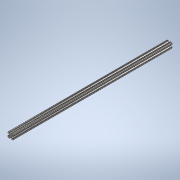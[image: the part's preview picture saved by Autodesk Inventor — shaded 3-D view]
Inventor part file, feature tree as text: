
AUTODESK INVENTOR PART (.ipt)
format: ipt  version: 2020 (Build 240168000, 168)  size: 238,080 bytes
history: native  units: in
note: dims shown in document units (in); Inventor stores cm internally (conversion verified against a paired STEP export)
features: extrude x1, sketch x1
ambient origin geometry x8: Origin, YZ Plane, XZ Plane, XY Plane, X Axis, Y Axis, Z Axis, Center Point
bodies: Solid1 (feature_tree)
feature tree (2):
  extrude  "Extrusion1"  [1 undecoded]
  sketch  "Sketch1"  dims[d0=30.0in d1=0.0in]
note: 1 required parameter value undecoded (feature->parameter linkage not recoverable at this tier; creation-order binding heuristic only, values carry confidence <= 0.55)
